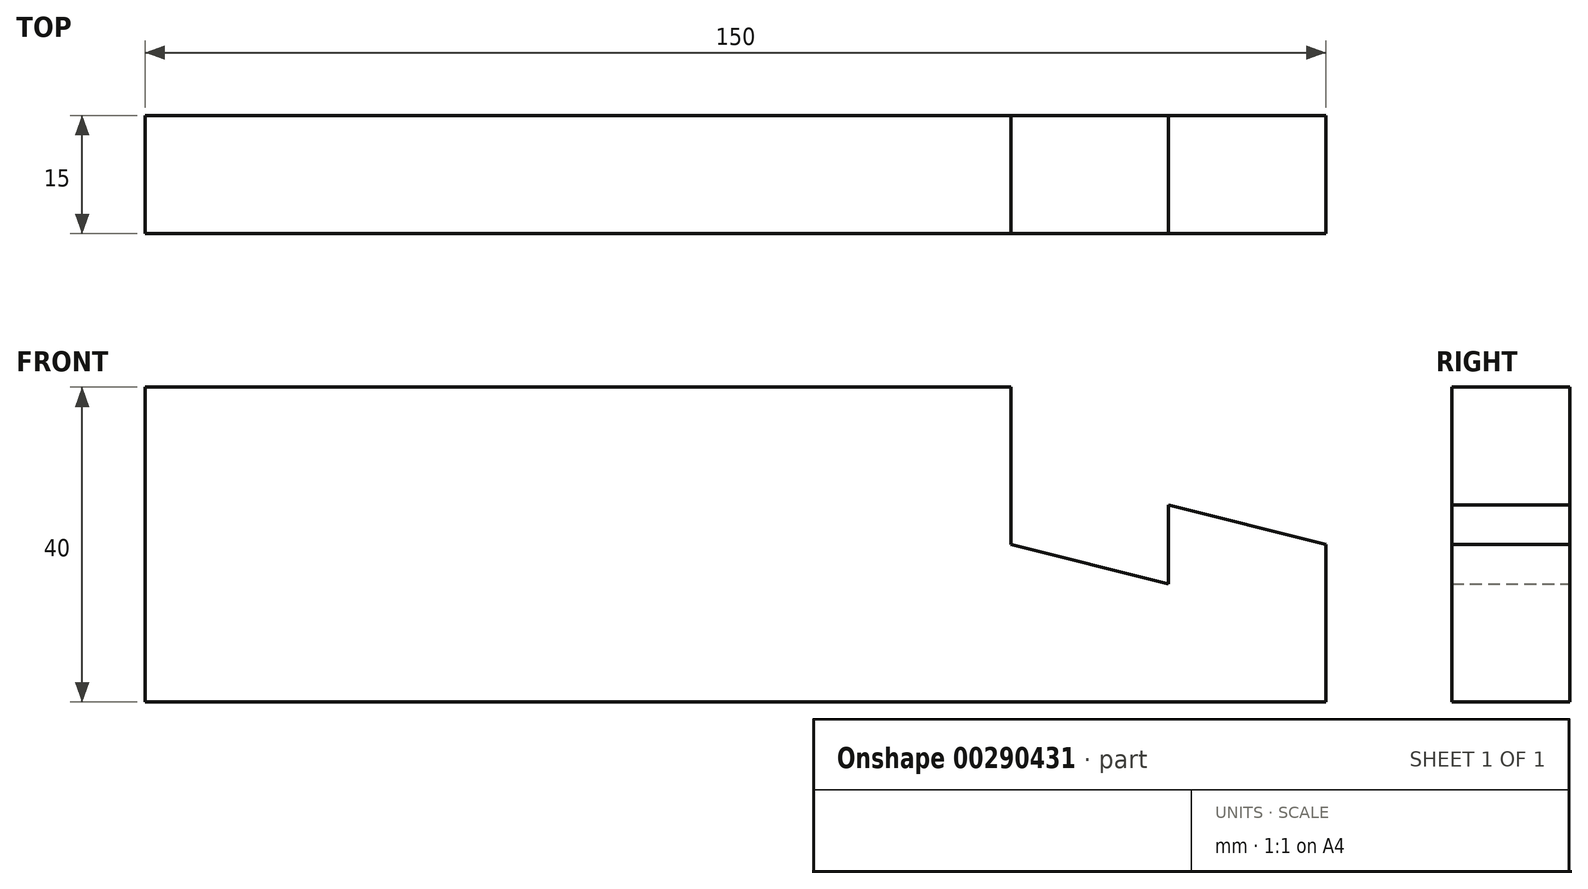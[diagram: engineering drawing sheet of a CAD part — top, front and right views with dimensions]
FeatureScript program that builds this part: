
annotation { "Feature Type Name" : "Feature", "Feature Type Description" : "" }
export const myFeature = defineFeature(function(context is Context, id is Id, definition is map)
    precondition{}
    {
        {
            var Q0;
            Q0=qCreatedBy(makeId("Front.planeOp"),FACE);
            var sketch = newSketch(context, id + "F0", { "sketchPlane" : qUnion([Q0])});
            skLineSegment(sketch, "E0", {"start": v(-75, 0) * mm, "end": v(75, 0) * mm});
            skLineSegment(sketch, "E1", {"start": v(75, 0) * mm, "end": v(75, 20) * mm});
            skLineSegment(sketch, "E2", {"start": v(75, 20) * mm, "end": v(55, 25) * mm});
            skLineSegment(sketch, "E3", {"start": v(55, 25) * mm, "end": v(55, 15) * mm});
            skLineSegment(sketch, "E4", {"start": v(55, 15) * mm, "end": v(35, 20) * mm});
            skLineSegment(sketch, "E5", {"start": v(35, 20) * mm, "end": v(35, 40) * mm});
            skLineSegment(sketch, "E6", {"start": v(35, 40) * mm, "end": v(-75, 40) * mm});
            skLineSegment(sketch, "E7", {"start": v(-75, 40) * mm, "end": v(-75, 0) * mm});
            skSolve(sketch);
        }
        {
            var Q0;
            Q0 = qSketchRegion(id + "F0", true);
            extrude(context, id + "F1", {"entities" : qUnion([Q0]), "endBound" : BoundingType.SYMMETRIC, "depth" : 15 * mm});
        }
    });
